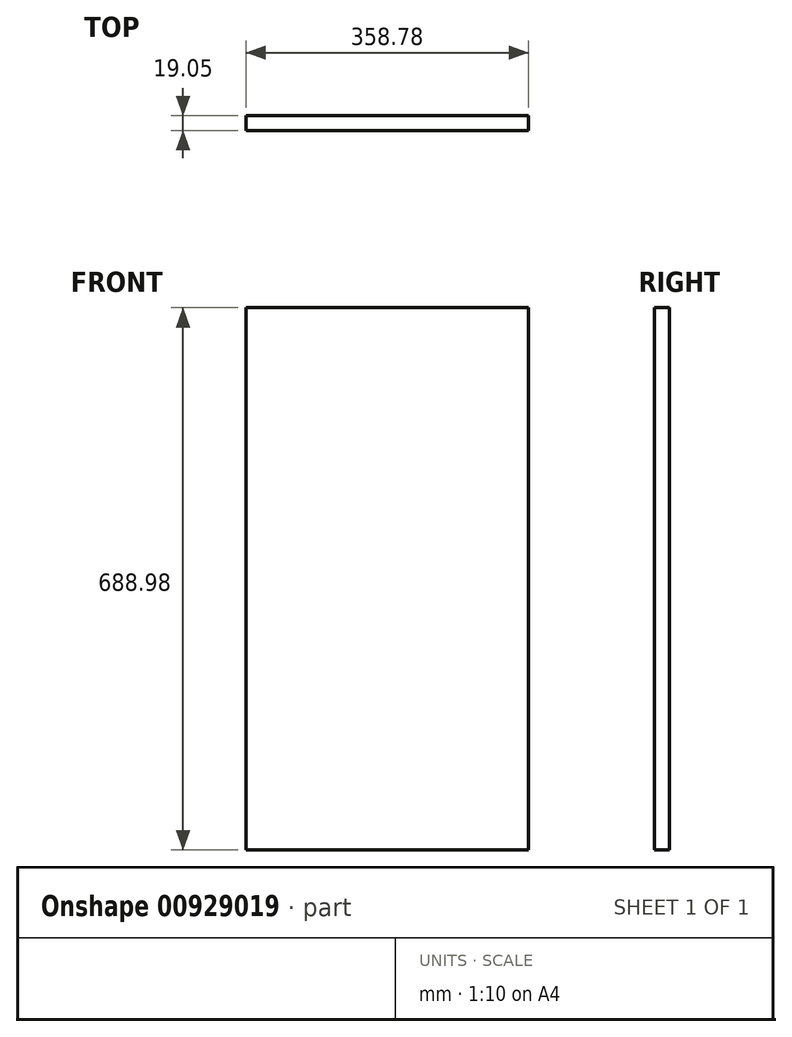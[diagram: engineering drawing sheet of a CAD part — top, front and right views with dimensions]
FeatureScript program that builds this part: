
annotation { "Feature Type Name" : "Feature", "Feature Type Description" : "" }
export const myFeature = defineFeature(function(context is Context, id is Id, definition is map)
    precondition{}
    {
        {
            var Q0;
            Q0=qCreatedBy(makeId("Front.planeOp"),FACE);
            var sketch = newSketch(context, id + "F0", { "sketchPlane" : qUnion([Q0])});
            skLineSegment(sketch, "E0.bottom", {"start": v(179.39, 344.49) * mm, "end": v(-179.39, 344.49) * mm});
            skLineSegment(sketch, "E0.top", {"start": v(179.39, -344.49) * mm, "end": v(-179.39, -344.49) * mm});
            skLineSegment(sketch, "E0.left", {"start": v(179.39, 344.49) * mm, "end": v(179.39, -344.49) * mm});
            skLineSegment(sketch, "E0.right", {"start": v(-179.39, 344.49) * mm, "end": v(-179.39, -344.49) * mm});
            skPoint(sketch, "E0.middle", {"position": v(0, 0) * mm});
            skSolve(sketch);
        }
        {
            var Q0;
            Q0=makeQuery(id+"F0.imprint","IMPRINT",FACE,{"disambiguationData":[TD([[makeQuery(id+"F0.imprint","IMPRINT",EDGE,{"derivedFrom":sQuery(id+"F0.wireOp",EDGE,"E0.bottom")}),1.0]])]});
            extrude(context, id + "F1", {"entities" : qUnion([Q0]), "depth" : 19.05 * mm, "offsetDistance" : 25.4 * mm});
        }
    });
